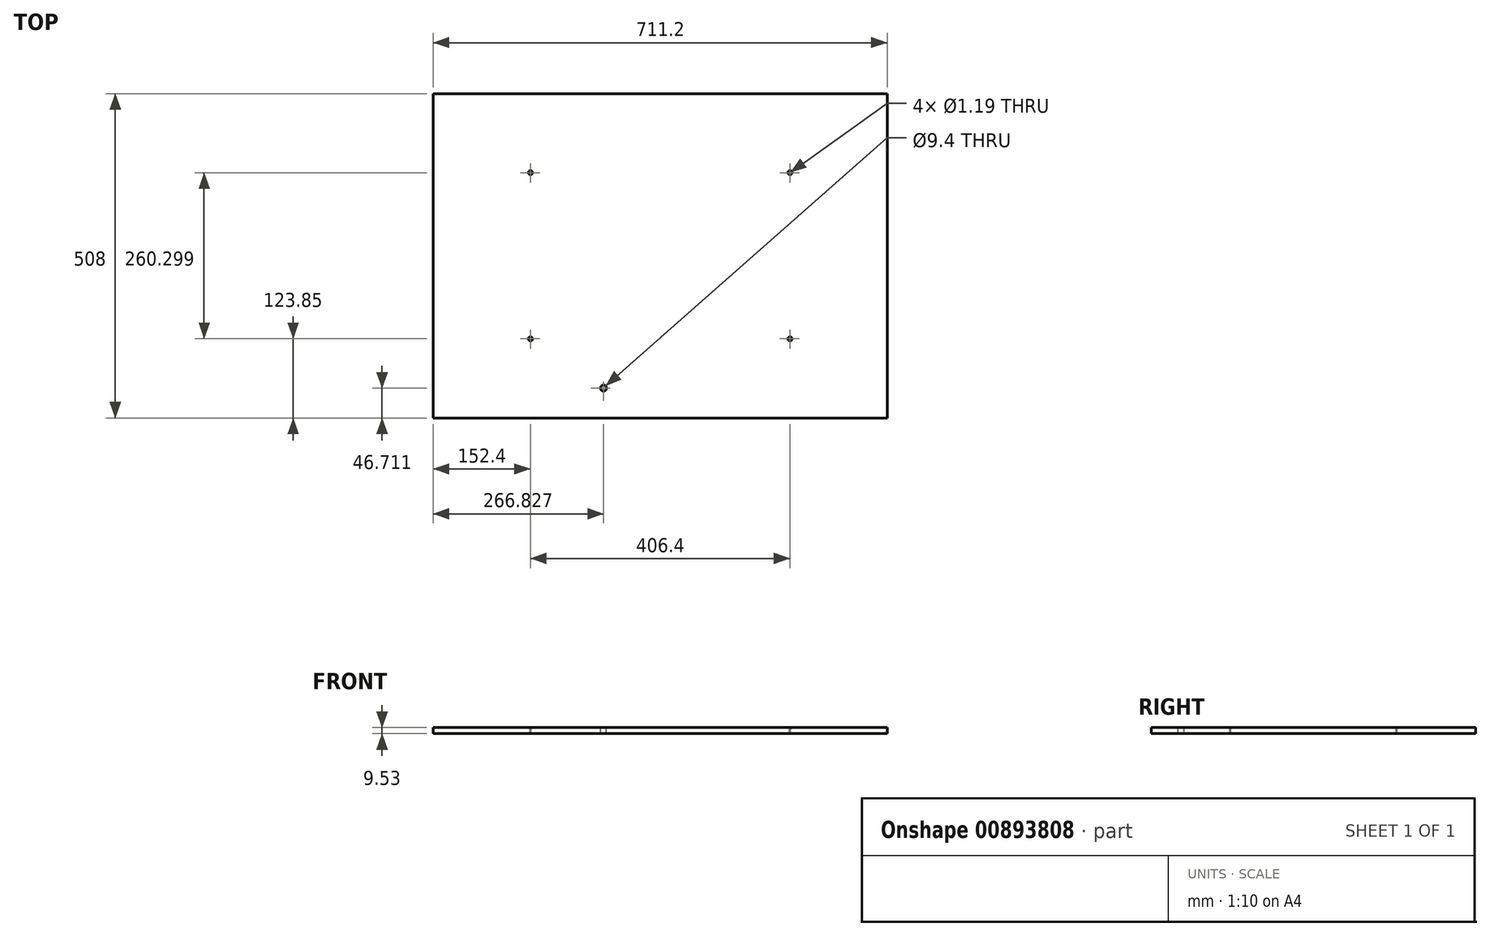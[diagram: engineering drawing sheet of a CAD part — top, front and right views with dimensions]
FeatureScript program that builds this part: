
annotation { "Feature Type Name" : "Feature", "Feature Type Description" : "" }
export const myFeature = defineFeature(function(context is Context, id is Id, definition is map)
    precondition{}
    {
        {
            var Q0;
            Q0=qCreatedBy(makeId("Top.planeOp"),FACE);
            var sketch = newSketch(context, id + "F0", { "sketchPlane" : qUnion([Q0])});
            skLineSegment(sketch, "E0.bottom", {"start": v(-355.6, 254) * mm, "end": v(355.6, 254) * mm});
            skLineSegment(sketch, "E0.top", {"start": v(-355.6, -254) * mm, "end": v(355.6, -254) * mm});
            skLineSegment(sketch, "E0.left", {"start": v(-355.6, 254) * mm, "end": v(-355.6, -254) * mm});
            skLineSegment(sketch, "E0.right", {"start": v(355.6, 254) * mm, "end": v(355.6, -254) * mm});
            skPoint(sketch, "E0.middle", {"position": v(0, 0) * mm});
            skSolve(sketch);
        }
        {
            var Q0;
            Q0 = qSketchRegion(id + "F0", true);
            extrude(context, id + "F1", {"entities" : qUnion([Q0]), "depth" : 9.52 * mm, "offsetDistance" : 25.4 * mm});
        }
        {
            var Q0;
            Q0=makeQuery(id+"F1.opExtrude","CAP_FACE",FACE,{"disambiguationData":[OSD([sQuery(id+"F0.wireOp",EDGE,"E0.bottom"),sQuery(id+"F0.wireOp",EDGE,"E0.top"),sQuery(id+"F0.wireOp",EDGE,"E0.left"),sQuery(id+"F0.wireOp",EDGE,"E0.right")])],"isStart":false});
            var sketch = newSketch(context, id + "F2", { "sketchPlane" : qUnion([Q0])});
            skPoint(sketch, "E1", {"position": v(-203.2, -130.15) * mm});
            skPoint(sketch, "E2", {"position": v(203.2, -130.15) * mm});
            skPoint(sketch, "E3", {"position": v(203.2, 130.15) * mm});
            skPoint(sketch, "E4", {"position": v(-203.2, 130.15) * mm});
            skSolve(sketch);
        }
        {
            var Q0;
            Q0=sQuery(id+"F2.wireOp",VERTEX,"E4");
            var Q1;
            Q1=sQuery(id+"F2.wireOp",VERTEX,"E1");
            var Q2;
            Q2=sQuery(id+"F2.wireOp",VERTEX,"E3");
            var Q3;
            Q3=sQuery(id+"F2.wireOp",VERTEX,"E2");
            var Q4;
            Q4=makeQuery(id+"F1.opExtrude","SWEPT_BODY",BODY,{"disambiguationData":[OSD([sQuery(id+"F0.wireOp",EDGE,"E0.bottom"),sQuery(id+"F0.wireOp",EDGE,"E0.top"),sQuery(id+"F0.wireOp",EDGE,"E0.left"),sQuery(id+"F0.wireOp",EDGE,"E0.right")])]});
            hole(context, id + "F3", {"style" : HoleStyle.C_SINK, "endStyle" : HoleEndStyle.THROUGH, "holeDiameter" : 1.2 * mm, "cSinkDiameter" : 6.35 * mm, "cSinkAngle" : 90 * degree, "majorDiameter" : 6.35 * mm, "isTappedThrough" : true, "tappedDepth" : 12.7 * mm, "tapClearance" : 3, "locations" : qUnion([Q0, Q1, Q2, Q3]), "scope" : qUnion([Q4])});
        }
        {
            var Q0;
            Q0=makeQuery(id+"F1.opExtrude","CAP_FACE",FACE,{"disambiguationData":[OSD([sQuery(id+"F0.wireOp",EDGE,"E0.bottom"),sQuery(id+"F0.wireOp",EDGE,"E0.top"),sQuery(id+"F0.wireOp",EDGE,"E0.left"),sQuery(id+"F0.wireOp",EDGE,"E0.right")])],"isStart":false});
            var sketch = newSketch(context, id + "F4", { "sketchPlane" : qUnion([Q0])});
            skPoint(sketch, "E5", {"position": v(-88.77, -207.29) * mm});
            skSolve(sketch);
        }
        {
            var Q0;
            Q0=sQuery(id+"F4.wireOp",VERTEX,"E5");
            var Q1;
            Q1=makeQuery(id+"F1.opExtrude","SWEPT_BODY",BODY,{"disambiguationData":[OSD([sQuery(id+"F0.wireOp",EDGE,"E0.bottom"),sQuery(id+"F0.wireOp",EDGE,"E0.top"),sQuery(id+"F0.wireOp",EDGE,"E0.left"),sQuery(id+"F0.wireOp",EDGE,"E0.right")])]});
            hole(context, id + "F5", {"style" : HoleStyle.SIMPLE, "endStyle" : HoleEndStyle.THROUGH, "holeDiameter" : 9.4 * mm, "majorDiameter" : 6.35 * mm, "isTappedThrough" : true, "tappedDepth" : 12.7 * mm, "tapClearance" : 3, "locations" : qUnion([Q0]), "scope" : qUnion([Q1])});
        }
    });
